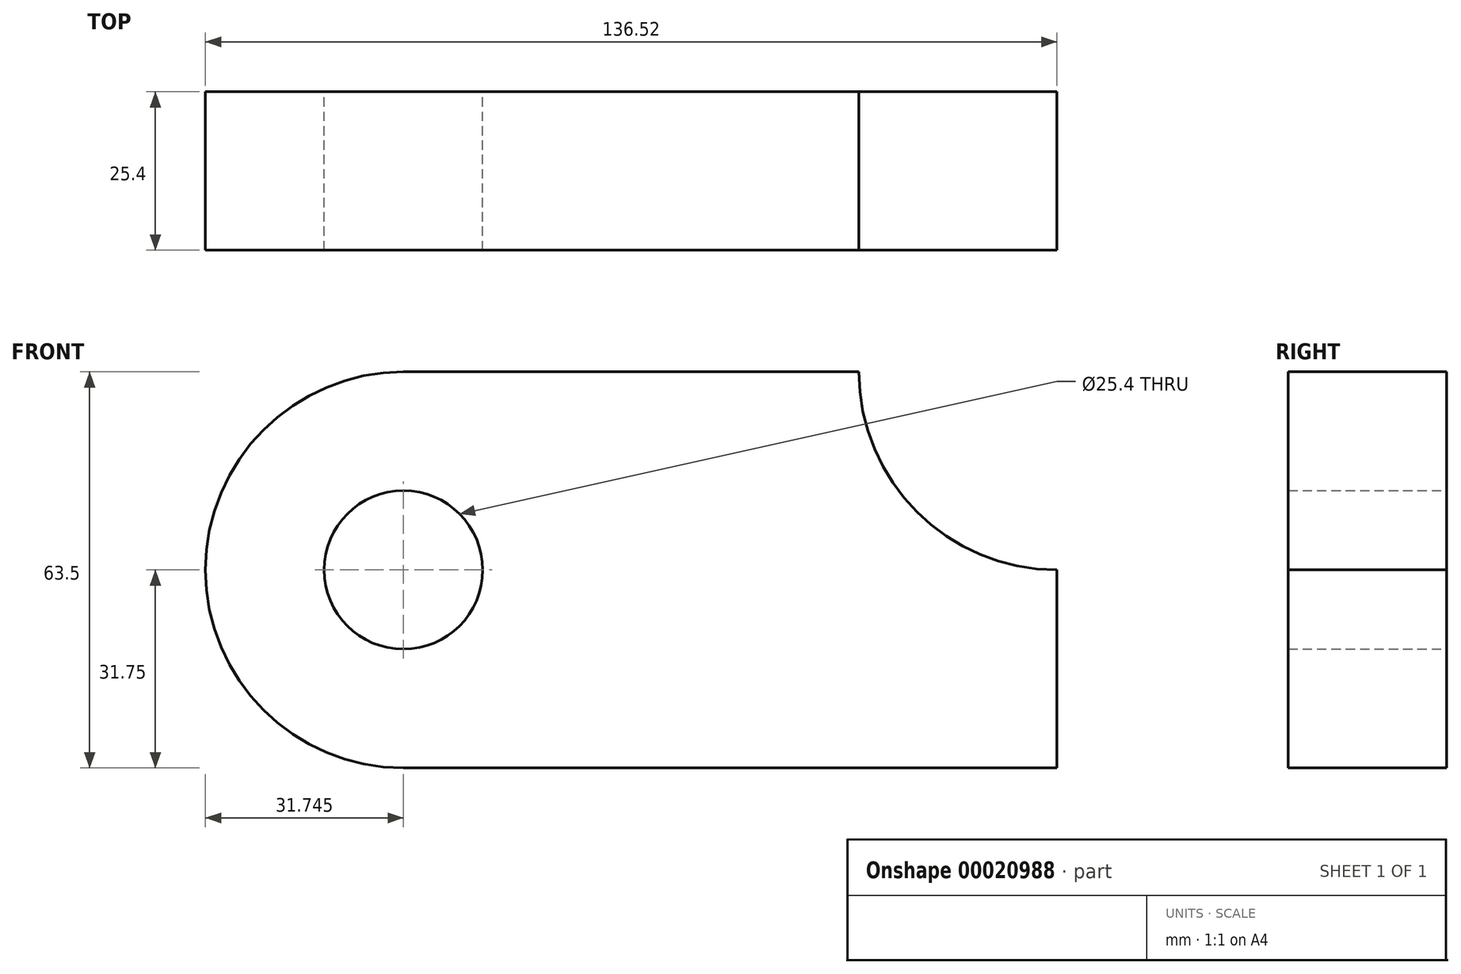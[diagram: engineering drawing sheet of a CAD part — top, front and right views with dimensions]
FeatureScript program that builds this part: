
annotation { "Feature Type Name" : "Feature", "Feature Type Description" : "" }
export const myFeature = defineFeature(function(context is Context, id is Id, definition is map)
    precondition{}
    {
        {
            var Q0;
            Q0=qCreatedBy(makeId("Front.planeOp"),FACE);
            var sketch = newSketch(context, id + "F0", { "sketchPlane" : qUnion([Q0])});
            skLineSegment(sketch, "E0.bottom", {"start": v(0, 0) * mm, "end": v(-104.77, 0) * mm});
            skLineSegment(sketch, "E0.top", {"start": v(0, 63.5) * mm, "end": v(-104.77, 63.5) * mm});
            skLineSegment(sketch, "E0.left", {"start": v(0, 0) * mm, "end": v(0, 63.5) * mm});
            skLineSegment(sketch, "E0.right", {"start": v(-104.78, 0) * mm, "end": v(-104.77, 63.5) * mm});
            skCircle(sketch, "E1", {"center": v(-104.77, 31.75) * mm, "radius": 31.75 * mm});
            skCircle(sketch, "E2", {"center": v(-104.77, 31.75) * mm, "radius": 12.7 * mm});
            skCircle(sketch, "E3", {"center": v(0, 63.5) * mm, "radius": 31.75 * mm});
            skSolve(sketch);
        }
        {
            var Q0;
            {var subQ4=sQuery(id+"F0.wireOp",EDGE,"E0.bottom");Q0=makeQuery(id+"F0.imprint","IMPRINT",FACE,{"disambiguationData":[TD([[makeQuery(id+"F0.imprint","IMPRINT",EDGE,{"derivedFrom":subQ4}),-1.0]])]});}
            var Q1;
            {var subQ0=sQuery(id+"F0.wireOp",EDGE,"E2");var subQ1=sQuery(id+"F0.wireOp",EDGE,"E0.right");var subQ3=makeQuery(id+"F0.imprint","INTERSECT",VERTEX,{"disambiguationData":[OD(0.0)],"derivedFrom":[subQ1,subQ0]});Q1=makeQuery(id+"F0.imprint","IMPRINT",FACE,{"disambiguationData":[TD([[makeQuery(id+"F0.imprint","IMPRINT",EDGE,{"disambiguationData":[TD([[subQ3,1.0]])],"derivedFrom":subQ0}),-1.0]])]});}
            var Q2;
            {var subQ0=sQuery(id+"F0.wireOp",EDGE,"E2");var subQ1=sQuery(id+"F0.wireOp",EDGE,"E0.right");var subQ3=makeQuery(id+"F0.imprint","INTERSECT",VERTEX,{"disambiguationData":[OD(0.0)],"derivedFrom":[subQ1,subQ0]});Q2=makeQuery(id+"F0.imprint","IMPRINT",FACE,{"disambiguationData":[TD([[makeQuery(id+"F0.imprint","IMPRINT",EDGE,{"disambiguationData":[TD([[subQ3,-1.0]])],"derivedFrom":subQ0}),-1.0]])]});}
            extrude(context, id + "F1", {"entities" : qUnion([Q0, Q1, Q2]), "depth" : 25.4 * mm});
        }
    });
